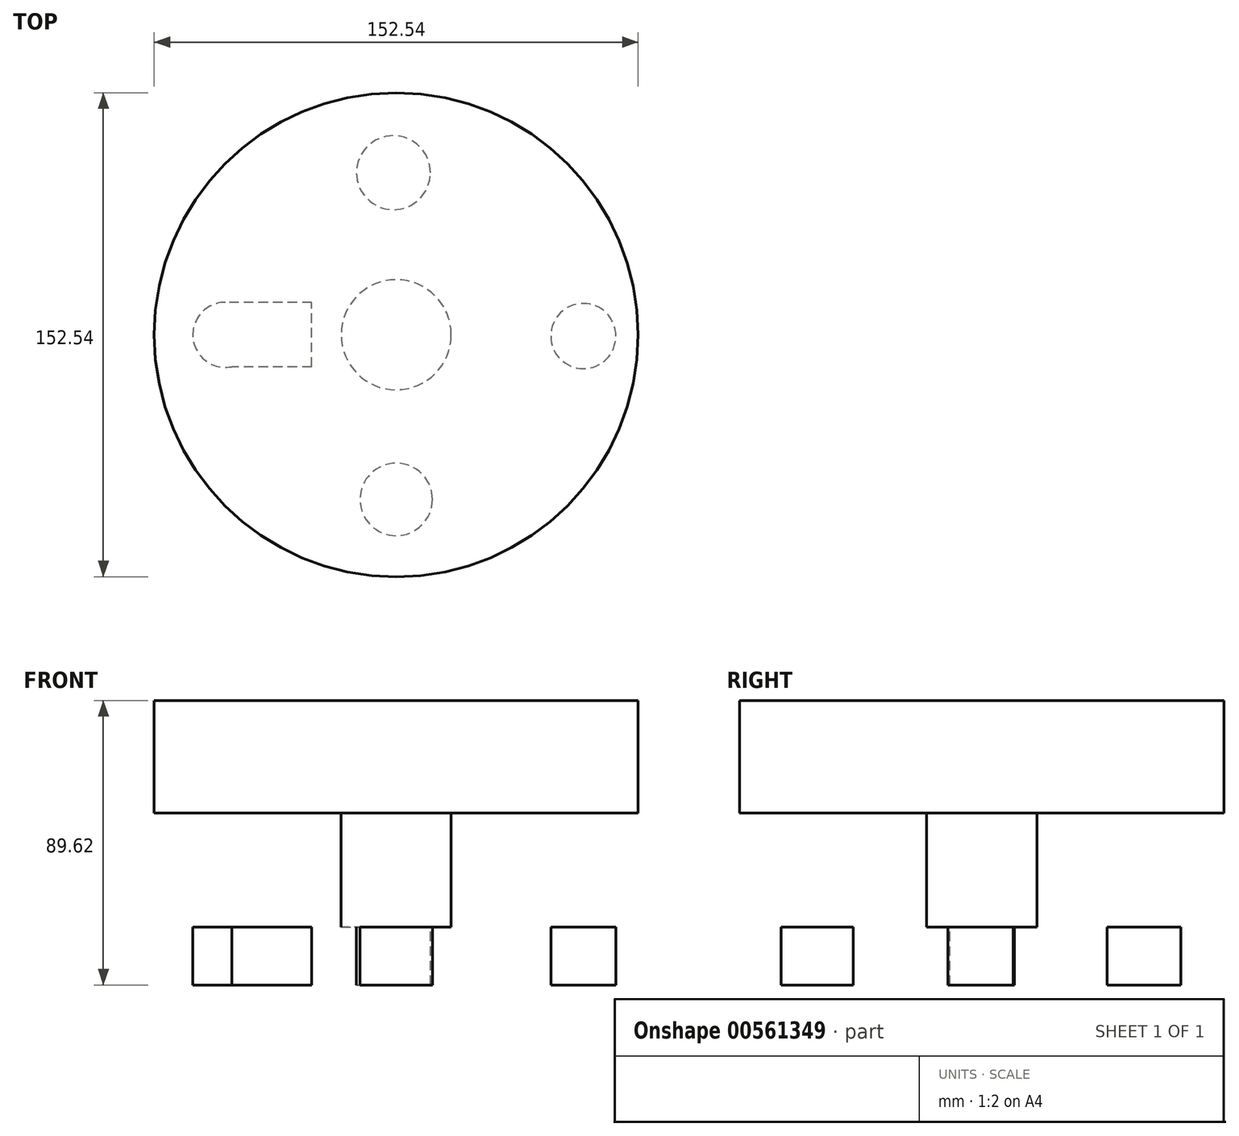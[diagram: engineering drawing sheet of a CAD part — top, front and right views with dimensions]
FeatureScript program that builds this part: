
annotation { "Feature Type Name" : "Feature", "Feature Type Description" : "" }
export const myFeature = defineFeature(function(context is Context, id is Id, definition is map)
    precondition{}
    {
        {
            var Q0;
            Q0=qCreatedBy(makeId("Front.planeOp"),FACE);
            var sketch = newSketch(context, id + "F0", { "sketchPlane" : qUnion([Q0])});
            skCircle(sketch, "E0", {"center": v(0, 0) * mm, "radius": 35.21 * mm});
            skLineSegment(sketch, "E1.bottom", {"start": v(0, 0) * mm, "end": v(76.27, 0) * mm});
            skLineSegment(sketch, "E1.top", {"start": v(0, 35.47) * mm, "end": v(76.27, 35.47) * mm});
            skLineSegment(sketch, "E1.left", {"start": v(0, 0) * mm, "end": v(0, 35.47) * mm});
            skLineSegment(sketch, "E1.right", {"start": v(76.27, 0) * mm, "end": v(76.27, 35.47) * mm});
            skSolve(sketch);
        }
        {
            var Q0;
            {var subQ0=sQuery(id+"F0.wireOp",EDGE,"E1.bottom");var subQ1=sQuery(id+"F0.wireOp",EDGE,"E0");var subQ2=makeQuery(id+"F0.imprint","INTERSECT",VERTEX,{"derivedFrom":[subQ1,subQ0]});Q0=makeQuery(id+"F0.imprint","IMPRINT",FACE,{"disambiguationData":[TD([[makeQuery(id+"F0.imprint","IMPRINT",EDGE,{"disambiguationData":[TD([[subQ2,-1.0]])],"derivedFrom":subQ1}),1.0]])]});}
            var Q1;
            {var subQ1=sQuery(id+"F0.wireOp",EDGE,"E1.top");Q1=makeQuery(id+"F0.imprint","IMPRINT",FACE,{"disambiguationData":[TD([[makeQuery(id+"F0.imprint","IMPRINT",EDGE,{"derivedFrom":subQ1}),-1.0]])]});}
            var Q2;
            Q2=sQuery(id+"F0.wireOp",EDGE,"E1.left");
            revolve(context, id + "F1", {"entities" : qUnion([Q0, Q1]), "axis" : qUnion([Q2]), "revolveType" : RevolveType.FULL});
        }
        {
            var Q0;
            Q0=qCreatedBy(makeId("Front.planeOp"),FACE);
            var sketch = newSketch(context, id + "F2", { "sketchPlane" : qUnion([Q0])});
            skLineSegment(sketch, "E2.bottom", {"start": v(0, 0) * mm, "end": v(17.34, 0) * mm});
            skLineSegment(sketch, "E2.top", {"start": v(0, -35.87) * mm, "end": v(17.34, -35.87) * mm});
            skLineSegment(sketch, "E2.left", {"start": v(0, 0) * mm, "end": v(0, -35.87) * mm});
            skLineSegment(sketch, "E2.right", {"start": v(17.34, 0) * mm, "end": v(17.34, -35.87) * mm});
            skSolve(sketch);
        }
        {
            var Q0;
            Q0=makeQuery(id+"F2.imprint","IMPRINT",FACE,{"disambiguationData":[TD([[makeQuery(id+"F2.imprint","IMPRINT",EDGE,{"derivedFrom":sQuery(id+"F2.wireOp",EDGE,"E2.bottom")}),-1.0]])]});
            var Q1;
            Q1=sQuery(id+"F2.wireOp",EDGE,"E2.left");
            revolve(context, id + "F3", {"operationType" : NewBodyOperationType.ADD, "entities" : qUnion([Q0]), "axis" : qUnion([Q1]), "revolveType" : RevolveType.FULL});
        }
        {
            var Q0;
            Q0=makeQuery(id+"F3.opRevolve","SWEPT_FACE",FACE,{"disambiguationData":[OSD([sQuery(id+"F2.wireOp",EDGE,"E2.top")])]});
            var sketch = newSketch(context, id + "F4", { "sketchPlane" : qUnion([Q0])});
            skLineSegment(sketch, "E3.bottom", {"start": v(28.8, 24.46) * mm, "end": v(-26.63, 24.46) * mm});
            skLineSegment(sketch, "E3.top", {"start": v(28.8, -24.06) * mm, "end": v(-26.63, -24.06) * mm});
            skLineSegment(sketch, "E3.left", {"start": v(28.8, 24.46) * mm, "end": v(28.8, -24.06) * mm});
            skLineSegment(sketch, "E3.right", {"start": v(-26.63, 24.46) * mm, "end": v(-26.63, -24.06) * mm});
            skLineSegment(sketch, "E4.bottom", {"start": v(28.8, 10.26) * mm, "end": v(58.97, 10.26) * mm});
            skLineSegment(sketch, "E4.top", {"start": v(28.8, -9.47) * mm, "end": v(58.97, -9.47) * mm});
            skLineSegment(sketch, "E4.left", {"start": v(28.8, 10.26) * mm, "end": v(28.8, -9.47) * mm});
            skLineSegment(sketch, "E4.right", {"start": v(58.97, 10.26) * mm, "end": v(58.97, -9.47) * mm});
            skLineSegment(sketch, "E5.bottom", {"start": v(-11.24, 24.46) * mm, "end": v(11.44, 24.46) * mm});
            skLineSegment(sketch, "E5.top", {"start": v(-11.24, 51.87) * mm, "end": v(11.44, 51.87) * mm});
            skLineSegment(sketch, "E5.left", {"start": v(-11.24, 24.46) * mm, "end": v(-11.24, 51.87) * mm});
            skLineSegment(sketch, "E5.right", {"start": v(11.44, 24.46) * mm, "end": v(11.44, 51.87) * mm});
            skLineSegment(sketch, "E6.bottom", {"start": v(-26.63, 10.06) * mm, "end": v(-53.85, 10.06) * mm});
            skLineSegment(sketch, "E6.top", {"start": v(-26.63, -10.26) * mm, "end": v(-53.85, -10.26) * mm});
            skLineSegment(sketch, "E6.left", {"start": v(-26.63, 10.06) * mm, "end": v(-26.63, -10.26) * mm});
            skLineSegment(sketch, "E6.right", {"start": v(-53.85, 10.06) * mm, "end": v(-53.85, -10.26) * mm});
            skLineSegment(sketch, "E7.bottom", {"start": v(-12.62, -24.06) * mm, "end": v(10.85, -24.06) * mm});
            skLineSegment(sketch, "E7.top", {"start": v(-12.62, -51.08) * mm, "end": v(10.85, -51.08) * mm});
            skLineSegment(sketch, "E7.left", {"start": v(-12.62, -24.06) * mm, "end": v(-12.62, -51.08) * mm});
            skLineSegment(sketch, "E7.right", {"start": v(10.85, -24.06) * mm, "end": v(10.85, -51.08) * mm});
            skCircle(sketch, "E8", {"center": v(0, 51.87) * mm, "radius": 11.41 * mm});
            skCircle(sketch, "E9", {"center": v(58.97, 0.4) * mm, "radius": 10.26 * mm});
            skCircle(sketch, "E10", {"center": v(-0.89, -51.08) * mm, "radius": 11.65 * mm});
            skCircle(sketch, "E11", {"center": v(-53.85, 0) * mm, "radius": 10.26 * mm});
            skSolve(sketch);
        }
        {
            var Q0;
            {var subQ0=sQuery(id+"F4.wireOp",EDGE,"E4.left");Q0=makeQuery(id+"F4.imprint","IMPRINT",FACE,{"disambiguationData":[TD([[makeQuery(id+"F4.imprint","IMPRINT",EDGE,{"derivedFrom":subQ0}),1.0]])]});}
            var Q1;
            {var subQ8=sQuery(id+"F4.wireOp",EDGE,"E4.left");Q1=makeQuery(id+"F4.imprint","IMPRINT",FACE,{"disambiguationData":[TD([[makeQuery(id+"F4.imprint","IMPRINT",EDGE,{"derivedFrom":subQ8}),-1.0]])]});}
            var Q2;
            Q2=makeQuery(id+"F4.imprint","IMPRINT",FACE,{"disambiguationData":[TD([[makeQuery(id+"F4.imprint","IMPRINT",EDGE,{"derivedFrom":sQuery(id+"F4.wireOp",EDGE,"E7.bottom")}),-1.0]])]});
            var Q3;
            {var subQ4=sQuery(id+"F4.wireOp",EDGE,"E6.top");Q3=makeQuery(id+"F4.imprint","IMPRINT",FACE,{"disambiguationData":[TD([[makeQuery(id+"F4.imprint","IMPRINT",EDGE,{"derivedFrom":subQ4}),-1.0]])]});}
            var Q4;
            {var subQ1=sQuery(id+"F4.wireOp",EDGE,"E5.bottom");Q4=makeQuery(id+"F4.imprint","IMPRINT",FACE,{"disambiguationData":[TD([[makeQuery(id+"F4.imprint","IMPRINT",EDGE,{"derivedFrom":subQ1}),1.0]])]});}
            var Q5;
            {var subQ0=sQuery(id+"F4.wireOp",EDGE,"E4.right");Q5=makeQuery(id+"F4.imprint","IMPRINT",FACE,{"disambiguationData":[TD([[makeQuery(id+"F4.imprint","IMPRINT",EDGE,{"derivedFrom":subQ0}),1.0]])]});}
            var Q6;
            {var subQ0=sQuery(id+"F4.wireOp",EDGE,"E10");var subQ1=sQuery(id+"F4.wireOp",EDGE,"E7.top");var subQ2=makeQuery(id+"F4.imprint","INTERSECT",VERTEX,{"disambiguationData":[OD(0.0)],"derivedFrom":[subQ1,subQ0]});Q6=makeQuery(id+"F4.imprint","IMPRINT",FACE,{"disambiguationData":[TD([[makeQuery(id+"F4.imprint","IMPRINT",EDGE,{"disambiguationData":[TD([[subQ2,-1.0]])],"derivedFrom":subQ1}),-1.0]])]});}
            var Q7;
            {var subQ0=sQuery(id+"F4.wireOp",EDGE,"E6.right");Q7=makeQuery(id+"F4.imprint","IMPRINT",FACE,{"disambiguationData":[TD([[makeQuery(id+"F4.imprint","IMPRINT",EDGE,{"derivedFrom":subQ0}),-1.0]])]});}
            var Q8;
            {var subQ0=sQuery(id+"F4.wireOp",EDGE,"E10");var subQ1=sQuery(id+"F4.wireOp",EDGE,"E7.top");var subQ2=makeQuery(id+"F4.imprint","INTERSECT",VERTEX,{"disambiguationData":[OD(0.0)],"derivedFrom":[subQ1,subQ0]});Q8=makeQuery(id+"F4.imprint","IMPRINT",FACE,{"disambiguationData":[TD([[makeQuery(id+"F4.imprint","IMPRINT",EDGE,{"disambiguationData":[TD([[subQ2,-1.0]])],"derivedFrom":subQ1}),1.0]])]});}
            var Q9;
            {var subQ0=sQuery(id+"F4.wireOp",EDGE,"E4.right");Q9=makeQuery(id+"F4.imprint","IMPRINT",FACE,{"disambiguationData":[TD([[makeQuery(id+"F4.imprint","IMPRINT",EDGE,{"derivedFrom":subQ0}),-1.0]])]});}
            var Q10;
            {var subQ0=sQuery(id+"F4.wireOp",EDGE,"E5.left");var subQ1=sQuery(id+"F4.wireOp",EDGE,"E5.top");var subQ2=makeQuery(id+"F4.imprint","INTERSECT",VERTEX,{"derivedFrom":[subQ1,subQ0]});Q10=makeQuery(id+"F4.imprint","IMPRINT",FACE,{"disambiguationData":[TD([[makeQuery(id+"F4.imprint","IMPRINT",EDGE,{"disambiguationData":[TD([[subQ2,-1.0]])],"derivedFrom":subQ1}),-1.0]])]});}
            var Q11;
            {var subQ0=sQuery(id+"F4.wireOp",EDGE,"E5.left");var subQ1=sQuery(id+"F4.wireOp",EDGE,"E5.top");var subQ2=makeQuery(id+"F4.imprint","INTERSECT",VERTEX,{"derivedFrom":[subQ1,subQ0]});Q11=makeQuery(id+"F4.imprint","IMPRINT",FACE,{"disambiguationData":[TD([[makeQuery(id+"F4.imprint","IMPRINT",EDGE,{"disambiguationData":[TD([[subQ2,-1.0]])],"derivedFrom":subQ1}),1.0]])]});}
            var Q12;
            {var subQ0=sQuery(id+"F4.wireOp",EDGE,"E6.right");Q12=makeQuery(id+"F4.imprint","IMPRINT",FACE,{"disambiguationData":[TD([[makeQuery(id+"F4.imprint","IMPRINT",EDGE,{"derivedFrom":subQ0}),1.0]])]});}
            extrude(context, id + "F5", {"entities" : qUnion([Q0, Q1, Q2, Q3, Q4, Q5, Q6, Q7, Q8, Q9, Q10, Q11, Q12]), "depth" : 18.29 * mm, "offsetDistance" : 25.4 * mm});
        }
        {
            var Q0;
            Q0=makeQuery(id+"F3.opRevolve","SWEPT_FACE",FACE,{"disambiguationData":[OSD([sQuery(id+"F2.wireOp",EDGE,"E2.top")])]});
            var sketch = newSketch(context, id + "F6", { "sketchPlane" : qUnion([Q0])});
            skCircle(sketch, "E12", {"center": v(0, 0) * mm, "radius": 17.55 * mm});
            skSolve(sketch);
        }
        {
            var Q0;
            Q0=sQuery(id+"F6.wireOp",EDGE,"E12");
            extrude(context, id + "F7", {"bodyType" : ToolBodyType.SURFACE, "surfaceEntities" : qUnion([Q0]), "depth" : 17.53 * mm, "offsetDistance" : 25.4 * mm});
        }
    });
